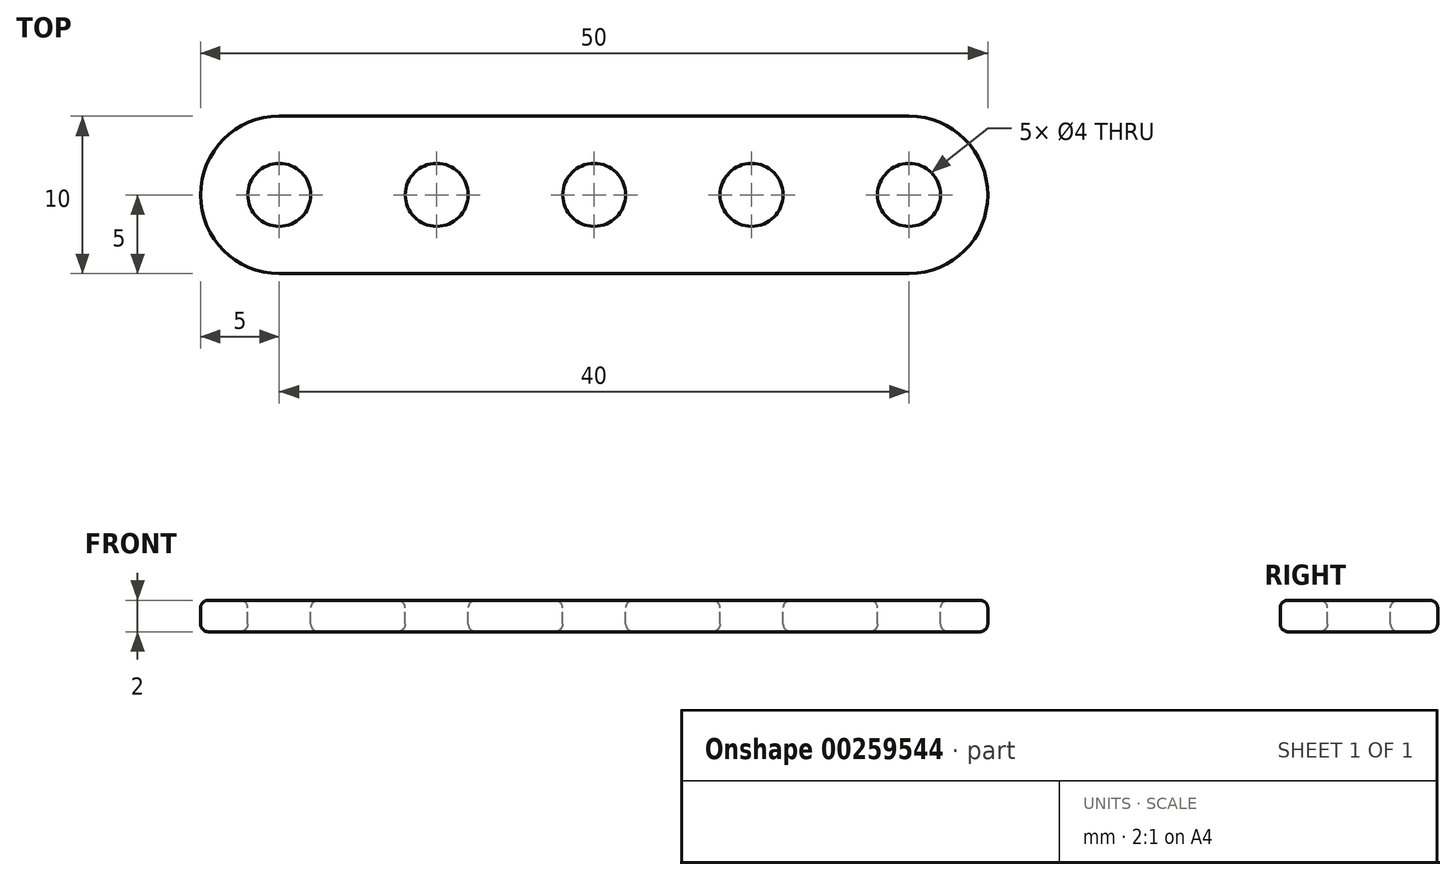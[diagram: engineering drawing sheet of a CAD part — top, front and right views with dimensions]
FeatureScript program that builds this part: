
annotation { "Feature Type Name" : "Feature", "Feature Type Description" : "" }
export const myFeature = defineFeature(function(context is Context, id is Id, definition is map)
    precondition{}
    {
        {
            var Q0;
            Q0=qCreatedBy(makeId("Top.planeOp"),FACE);
            var sketch = newSketch(context, id + "F3", { "sketchPlane" : qUnion([Q0])});
            skCircle(sketch, "E0", {"center": v(0, 0) * mm, "radius": 2 * mm});
            skCircle(sketch, "E1.1.0.0", {"center": v(10, 0) * mm, "radius": 2 * mm});
            skCircle(sketch, "E1.2.0.0", {"center": v(20, 0) * mm, "radius": 2 * mm});
            skLineSegment(sketch, "E1.direction1", {"start": v(0, 0) * mm, "end": v(10, 0) * mm, "construction": true});
            skCircle(sketch, "E2.1.0.0", {"center": v(-10, 0) * mm, "radius": 2 * mm});
            skCircle(sketch, "E2.2.0.0", {"center": v(-20, 0) * mm, "radius": 2 * mm});
            skLineSegment(sketch, "E2.direction1", {"start": v(0, 0) * mm, "end": v(-10, 0) * mm, "construction": true});
            skSolve(sketch);
        }
        {
            var Q0;
            Q0=qCreatedBy(makeId("Top.planeOp"),FACE);
            var sketch = newSketch(context, id + "F0", { "sketchPlane" : qUnion([Q0])});
            skLineSegment(sketch, "E3.bottom", {"start": v(25, 5) * mm, "end": v(-25, 5) * mm});
            skLineSegment(sketch, "E3.top", {"start": v(25, -5) * mm, "end": v(-25, -5) * mm});
            skLineSegment(sketch, "E3.left", {"start": v(25, 5) * mm, "end": v(25, -5) * mm});
            skLineSegment(sketch, "E3.right", {"start": v(-25, 5) * mm, "end": v(-25, -5) * mm});
            skPoint(sketch, "E3.middle", {"position": v(0, 0) * mm});
            skSolve(sketch);
        }
        {
            var Q0;
            Q0=makeQuery(id+"F0.imprint","IMPRINT",FACE,{"disambiguationData":[TD([[makeQuery(id+"F0.imprint","IMPRINT",EDGE,{"derivedFrom":sQuery(id+"F0.wireOp",EDGE,"E3.bottom")}),1.0]])]});
            extrude(context, id + "F1", {"entities" : qUnion([Q0]), "depth" : 2 * mm});
        }
        {
            var Q0;
            Q0=makeQuery(id+"F3.imprint","IMPRINT",FACE,{"disambiguationData":[TD([[makeQuery(id+"F3.imprint","IMPRINT",EDGE,{"derivedFrom":sQuery(id+"F3.wireOp",EDGE,"E2.2.0.0")}),1.0]])]});
            var Q1;
            Q1=makeQuery(id+"F3.imprint","IMPRINT",FACE,{"disambiguationData":[TD([[makeQuery(id+"F3.imprint","IMPRINT",EDGE,{"derivedFrom":sQuery(id+"F3.wireOp",EDGE,"E2.1.0.0")}),1.0]])]});
            var Q2;
            Q2=makeQuery(id+"F3.imprint","IMPRINT",FACE,{"disambiguationData":[TD([[makeQuery(id+"F3.imprint","IMPRINT",EDGE,{"derivedFrom":sQuery(id+"F3.wireOp",EDGE,"E0")}),1.0]])]});
            var Q3;
            Q3=makeQuery(id+"F3.imprint","IMPRINT",FACE,{"disambiguationData":[TD([[makeQuery(id+"F3.imprint","IMPRINT",EDGE,{"derivedFrom":sQuery(id+"F3.wireOp",EDGE,"E1.1.0.0")}),1.0]])]});
            var Q4;
            Q4=makeQuery(id+"F3.imprint","IMPRINT",FACE,{"disambiguationData":[TD([[makeQuery(id+"F3.imprint","IMPRINT",EDGE,{"derivedFrom":sQuery(id+"F3.wireOp",EDGE,"E1.2.0.0")}),1.0]])]});
            var Q5;
            Q5=sQuery(id+"F3.wireOp",EDGE,"E1.2.0.0");
            var Q6;
            Q6=sQuery(id+"F3.wireOp",EDGE,"E1.1.0.0");
            var Q7;
            Q7=sQuery(id+"F3.wireOp",EDGE,"E0");
            var Q8;
            Q8=sQuery(id+"F3.wireOp",EDGE,"E2.1.0.0");
            var Q9;
            Q9=sQuery(id+"F3.wireOp",EDGE,"E2.2.0.0");
            extrude(context, id + "F2", {"entities" : qUnion([Q0, Q1, Q2, Q3, Q4]), "operationType" : NewBodyOperationType.REMOVE, "surfaceEntities" : qUnion([Q5, Q6, Q7, Q8, Q9]), "oppositeDirection" : true, "depth" : 25 * mm});
        }
        {
            var Q0;
            Q0=makeQuery(id+"F1.opExtrude","SWEPT_EDGE",EDGE,{"disambiguationData":[OSD([sQuery(id+"F0.wireOp",EDGE,"E3.top"),sQuery(id+"F0.wireOp",EDGE,"E3.left")])]});
            var Q1;
            Q1=makeQuery(id+"F1.opExtrude","SWEPT_EDGE",EDGE,{"disambiguationData":[OSD([sQuery(id+"F0.wireOp",EDGE,"E3.bottom"),sQuery(id+"F0.wireOp",EDGE,"E3.left")])]});
            var Q2;
            Q2=makeQuery(id+"F1.opExtrude","SWEPT_EDGE",EDGE,{"disambiguationData":[OSD([sQuery(id+"F0.wireOp",EDGE,"E3.top"),sQuery(id+"F0.wireOp",EDGE,"E3.right")])]});
            var Q3;
            Q3=makeQuery(id+"F1.opExtrude","SWEPT_EDGE",EDGE,{"disambiguationData":[OSD([sQuery(id+"F0.wireOp",EDGE,"E3.bottom"),sQuery(id+"F0.wireOp",EDGE,"E3.right")])]});
            fillet(context, id + "F4", {"entities" : qUnion([Q0, Q1, Q2, Q3]), "radius" : 5 * mm, "tangentPropagation" : true, "allowEdgeOverflow" : false});
        }
        {
            var Q0;
            Q0=makeQuery(id+"F1.opExtrude","CAP_FACE",FACE,{"disambiguationData":[OSD([sQuery(id+"F0.wireOp",EDGE,"E3.bottom"),sQuery(id+"F0.wireOp",EDGE,"E3.top"),sQuery(id+"F0.wireOp",EDGE,"E3.left"),sQuery(id+"F0.wireOp",EDGE,"E3.right")])],"isStart":false});
            var sketch = newSketch(context, id + "F5", { "sketchPlane" : qUnion([Q0])});
            skCircle(sketch, "E4", {"center": v(0, 0) * mm, "radius": 2 * mm});
            skCircle(sketch, "E5.1.0.0", {"center": v(10, 0) * mm, "radius": 2 * mm});
            skCircle(sketch, "E5.2.0.0", {"center": v(20, 0) * mm, "radius": 2 * mm});
            skLineSegment(sketch, "E5.direction1", {"start": v(0, 0) * mm, "end": v(10, 0) * mm, "construction": true});
            skCircle(sketch, "E6.1.0.0", {"center": v(-10, 0) * mm, "radius": 2 * mm});
            skCircle(sketch, "E6.2.0.0", {"center": v(-20, 0) * mm, "radius": 2 * mm});
            skLineSegment(sketch, "E6.direction1", {"start": v(0, 0) * mm, "end": v(-10, 0) * mm, "construction": true});
            skSolve(sketch);
        }
        {
            var Q0;
            Q0=makeQuery(id+"F5.imprint","IMPRINT",FACE,{"disambiguationData":[TD([[makeQuery(id+"F5.imprint","IMPRINT",EDGE,{"derivedFrom":sQuery(id+"F5.wireOp",EDGE,"E5.2.0.0")}),1.0]])]});
            var Q1;
            Q1=makeQuery(id+"F5.imprint","IMPRINT",FACE,{"disambiguationData":[TD([[makeQuery(id+"F5.imprint","IMPRINT",EDGE,{"derivedFrom":sQuery(id+"F5.wireOp",EDGE,"E5.1.0.0")}),1.0]])]});
            var Q2;
            Q2=makeQuery(id+"F5.imprint","IMPRINT",FACE,{"disambiguationData":[TD([[makeQuery(id+"F5.imprint","IMPRINT",EDGE,{"derivedFrom":sQuery(id+"F5.wireOp",EDGE,"E4")}),1.0]])]});
            var Q3;
            Q3=makeQuery(id+"F5.imprint","IMPRINT",FACE,{"disambiguationData":[TD([[makeQuery(id+"F5.imprint","IMPRINT",EDGE,{"derivedFrom":sQuery(id+"F5.wireOp",EDGE,"E6.1.0.0")}),1.0]])]});
            var Q4;
            Q4=makeQuery(id+"F5.imprint","IMPRINT",FACE,{"disambiguationData":[TD([[makeQuery(id+"F5.imprint","IMPRINT",EDGE,{"derivedFrom":sQuery(id+"F5.wireOp",EDGE,"E6.2.0.0")}),1.0]])]});
            extrude(context, id + "F6", {"entities" : qUnion([Q0, Q1, Q2, Q3, Q4]), "operationType" : NewBodyOperationType.REMOVE, "oppositeDirection" : true, "depth" : 25 * mm});
        }
        {
            var Q0;
            Q0=makeQuery(id+"F1.opExtrude","CAP_FACE",FACE,{"disambiguationData":[OSD([sQuery(id+"F0.wireOp",EDGE,"E3.bottom"),sQuery(id+"F0.wireOp",EDGE,"E3.top"),sQuery(id+"F0.wireOp",EDGE,"E3.left"),sQuery(id+"F0.wireOp",EDGE,"E3.right")])],"isStart":false});
            var Q1;
            Q1=makeQuery(id+"F1.opExtrude","CAP_FACE",FACE,{"disambiguationData":[OSD([sQuery(id+"F0.wireOp",EDGE,"E3.bottom"),sQuery(id+"F0.wireOp",EDGE,"E3.top"),sQuery(id+"F0.wireOp",EDGE,"E3.left"),sQuery(id+"F0.wireOp",EDGE,"E3.right")])],"isStart":true});
            fillet(context, id + "F7", {"entities" : qUnion([Q0, Q1]), "radius" : 0.5 * mm, "tangentPropagation" : true, "allowEdgeOverflow" : false});
        }
    });
